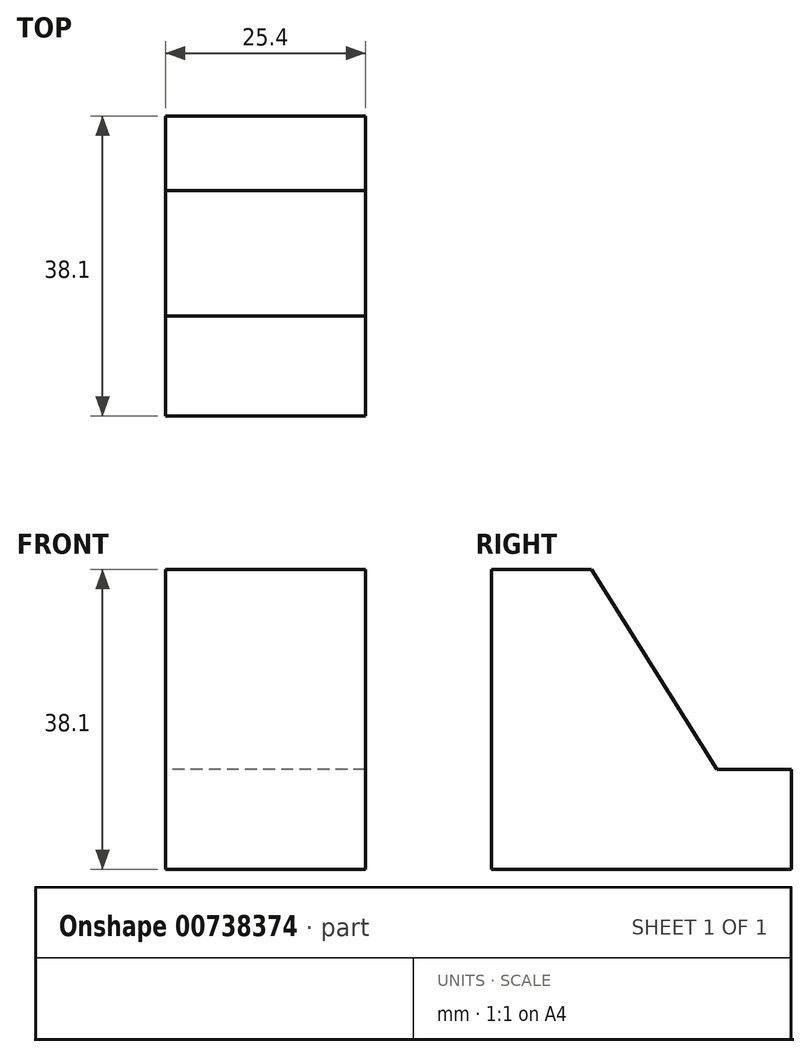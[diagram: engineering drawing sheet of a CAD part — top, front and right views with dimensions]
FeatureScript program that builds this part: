
annotation { "Feature Type Name" : "Feature", "Feature Type Description" : "" }
export const myFeature = defineFeature(function(context is Context, id is Id, definition is map)
    precondition{}
    {
        {
            var Q0;
            Q0=qCreatedBy(makeId("Right.planeOp"),FACE);
            var sketch = newSketch(context, id + "F0", { "sketchPlane" : qUnion([Q0])});
            skLineSegment(sketch, "E0", {"start": v(0, 0) * mm, "end": v(0, 38.1) * mm});
            skLineSegment(sketch, "E1", {"start": v(0, 38.1) * mm, "end": v(12.7, 38.1) * mm});
            skLineSegment(sketch, "E2", {"start": v(12.7, 38.1) * mm, "end": v(28.66, 12.7) * mm});
            skLineSegment(sketch, "E3", {"start": v(28.66, 12.7) * mm, "end": v(38.1, 12.7) * mm});
            skLineSegment(sketch, "E4", {"start": v(38.1, 12.7) * mm, "end": v(38.1, 0) * mm});
            skLineSegment(sketch, "E5", {"start": v(38.1, 0) * mm, "end": v(0, 0) * mm});
            skSolve(sketch);
        }
        {
            var Q0;
            Q0=makeQuery(id+"F0.imprint","IMPRINT",FACE,{"disambiguationData":[TD([[makeQuery(id+"F0.imprint","IMPRINT",EDGE,{"derivedFrom":sQuery(id+"F0.wireOp",EDGE,"E0")}),-1.0]])]});
            extrude(context, id + "F1", {"entities" : qUnion([Q0]), "depth" : 25.4 * mm, "offsetDistance" : 25.4 * mm});
        }
    });
